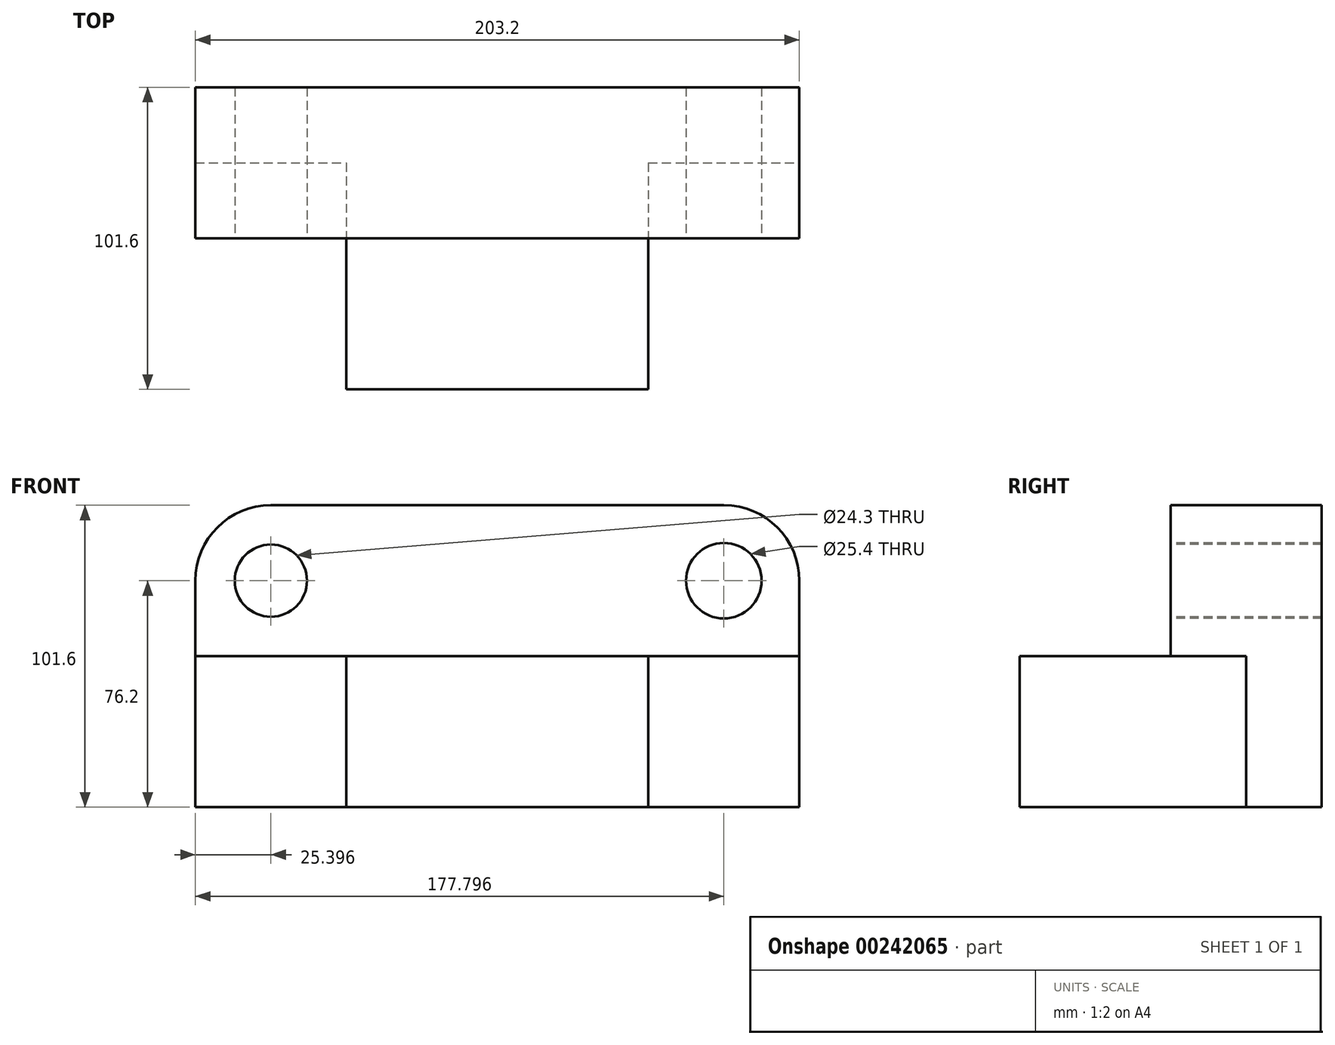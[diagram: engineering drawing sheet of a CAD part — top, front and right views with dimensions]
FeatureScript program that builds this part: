
annotation { "Feature Type Name" : "Feature", "Feature Type Description" : "" }
export const myFeature = defineFeature(function(context is Context, id is Id, definition is map)
    precondition{}
    {
        {
            var Q0;
            Q0=qCreatedBy(makeId("Top.planeOp"),FACE);
            var sketch = newSketch(context, id + "F0", { "sketchPlane" : qUnion([Q0])});
            skLineSegment(sketch, "E0.bottom", {"start": v(-154.2, -86.22) * mm, "end": v(49, -86.22) * mm});
            skLineSegment(sketch, "E0.top", {"start": v(-154.2, 15.38) * mm, "end": v(49, 15.38) * mm});
            skLineSegment(sketch, "E0.left", {"start": v(-154.2, -86.22) * mm, "end": v(-154.2, 15.38) * mm});
            skLineSegment(sketch, "E0.right", {"start": v(49, -86.22) * mm, "end": v(49, 15.38) * mm});
            skSolve(sketch);
        }
        {
            var Q0;
            Q0 = qSketchRegion(id + "F0", true);
            extrude(context, id + "F1", {"entities" : qUnion([Q0]), "depth" : 76.2 * mm});
        }
        {
            var Q0;
            Q0=makeQuery(id+"F1.opExtrude","SWEPT_FACE",FACE,{"disambiguationData":[OSD([sQuery(id+"F0.wireOp",EDGE,"E0.bottom")])]});
            var sketch = newSketch(context, id + "F2", { "sketchPlane" : qUnion([Q0])});
            skLineSegment(sketch, "E1", {"start": v(49, 0) * mm, "end": v(-1.8, 0) * mm});
            skLineSegment(sketch, "E2", {"start": v(-1.8, 0) * mm, "end": v(-1.8, 50.8) * mm});
            skLineSegment(sketch, "E3", {"start": v(-1.8, 50.8) * mm, "end": v(49, 50.8) * mm});
            skLineSegment(sketch, "E4", {"start": v(49, 50.8) * mm, "end": v(49, 0) * mm});
            skSolve(sketch);
        }
        {
            var Q0;
            Q0 = qSketchRegion(id + "F2", true);
            extrude(context, id + "F3", {"entities" : qUnion([Q0]), "operationType" : NewBodyOperationType.REMOVE, "oppositeDirection" : true, "depth" : 76.2 * mm});
        }
        {
            var Q0;
            Q0=makeQuery(id+"F1.opExtrude","SWEPT_FACE",FACE,{"disambiguationData":[OSD([sQuery(id+"F0.wireOp",EDGE,"E0.bottom")])]});
            var sketch = newSketch(context, id + "F4", { "sketchPlane" : qUnion([Q0])});
            skLineSegment(sketch, "E5", {"start": v(-1.8, 50.8) * mm, "end": v(-1.8, 76.2) * mm});
            skLineSegment(sketch, "E6", {"start": v(-1.8, 76.2) * mm, "end": v(49, 76.2) * mm});
            skLineSegment(sketch, "E7", {"start": v(-1.8, 50.8) * mm, "end": v(49, 50.8) * mm});
            skLineSegment(sketch, "E8", {"start": v(49, 76.2) * mm, "end": v(49, 50.8) * mm});
            skSolve(sketch);
        }
        {
            var Q0;
            Q0 = qSketchRegion(id + "F4", true);
            extrude(context, id + "F5", {"entities" : qUnion([Q0]), "operationType" : NewBodyOperationType.REMOVE, "oppositeDirection" : true, "depth" : 50.8 * mm});
        }
        {
            var Q0;
            Q0=makeQuery(id+"F1.opExtrude","SWEPT_FACE",FACE,{"disambiguationData":[OSD([sQuery(id+"F0.wireOp",EDGE,"E0.bottom")])]});
            var sketch = newSketch(context, id + "F6", { "sketchPlane" : qUnion([Q0])});
            skLineSegment(sketch, "E9", {"start": v(-154.2, 76.2) * mm, "end": v(-154.2, 50.8) * mm});
            skLineSegment(sketch, "E10", {"start": v(-154.2, 50.8) * mm, "end": v(-1.8, 50.8) * mm});
            skLineSegment(sketch, "E11", {"start": v(-1.8, 76.2) * mm, "end": v(-1.8, 50.8) * mm});
            skLineSegment(sketch, "E12", {"start": v(-154.2, 76.2) * mm, "end": v(-1.8, 76.2) * mm});
            skSolve(sketch);
        }
        {
            var Q0;
            Q0 = qSketchRegion(id + "F6", true);
            extrude(context, id + "F7", {"entities" : qUnion([Q0]), "operationType" : NewBodyOperationType.REMOVE, "oppositeDirection" : true, "depth" : 50.8 * mm});
        }
        {
            var Q0;
            Q0=makeQuery(id+"F1.opExtrude","SWEPT_FACE",FACE,{"disambiguationData":[OSD([sQuery(id+"F0.wireOp",EDGE,"E0.bottom")])]});
            var sketch = newSketch(context, id + "F8", { "sketchPlane" : qUnion([Q0])});
            skLineSegment(sketch, "E13", {"start": v(-154.2, 50.8) * mm, "end": v(-154.2, 0) * mm});
            skLineSegment(sketch, "E14", {"start": v(-154.2, 50.8) * mm, "end": v(-103.4, 50.8) * mm});
            skLineSegment(sketch, "E15", {"start": v(-103.4, 50.8) * mm, "end": v(-103.4, 0) * mm});
            skLineSegment(sketch, "E16", {"start": v(-154.2, 0) * mm, "end": v(-103.4, 0) * mm});
            skSolve(sketch);
        }
        {
            var Q0;
            Q0 = qSketchRegion(id + "F8", true);
            extrude(context, id + "F9", {"entities" : qUnion([Q0]), "operationType" : NewBodyOperationType.REMOVE, "oppositeDirection" : true, "depth" : 76.2 * mm});
        }
        {
            var Q0;
            Q0=makeQuery(id+"F1.opExtrude","CAP_FACE",FACE,{"disambiguationData":[OSD([sQuery(id+"F0.wireOp",EDGE,"E0.bottom"),sQuery(id+"F0.wireOp",EDGE,"E0.top"),sQuery(id+"F0.wireOp",EDGE,"E0.left"),sQuery(id+"F0.wireOp",EDGE,"E0.right")])],"isStart":false});
            var sketch = newSketch(context, id + "F10", { "sketchPlane" : qUnion([Q0])});
            skLineSegment(sketch, "E17.bottom", {"start": v(-154.2, -35.42) * mm, "end": v(49, -35.42) * mm});
            skLineSegment(sketch, "E17.top", {"start": v(-154.2, 15.38) * mm, "end": v(49, 15.38) * mm});
            skLineSegment(sketch, "E17.left", {"start": v(-154.2, -35.42) * mm, "end": v(-154.2, 15.38) * mm});
            skLineSegment(sketch, "E17.right", {"start": v(49, -35.42) * mm, "end": v(49, 15.38) * mm});
            skSolve(sketch);
        }
        {
            var Q0;
            Q0 = qSketchRegion(id + "F10", true);
            extrude(context, id + "F11", {"entities" : qUnion([Q0]), "operationType" : NewBodyOperationType.ADD, "depth" : 25.4 * mm});
        }
        {
            var Q0;
            Q0=makeQuery(id+"F11.opExtrude","CAP_EDGE",EDGE,{"disambiguationData":[OSD([sQuery(id+"F10.wireOp",EDGE,"E17.left")])],"isStart":false});
            fillet(context, id + "F12", {"entities" : qUnion([Q0]), "radius" : 25.4 * mm, "tangentPropagation" : true, "allowEdgeOverflow" : false});
        }
        {
            var Q0;
            Q0=makeQuery(id+"F11.opExtrude","CAP_EDGE",EDGE,{"disambiguationData":[OSD([sQuery(id+"F10.wireOp",EDGE,"E17.right")])],"isStart":false});
            fillet(context, id + "F13", {"entities" : qUnion([Q0]), "radius" : 25.4 * mm, "tangentPropagation" : true, "allowEdgeOverflow" : false});
        }
        {
            var Q0;
            Q0=makeQuery(id+"F11.boolean.opBoolean","MERGE",FACE,{"derivedFrom":[makeQuery(id+"F7.boolean.opBoolean","MERGE",FACE,{"derivedFrom":[makeQuery(id+"F5.boolean.opBoolean","COPY",FACE,{"derivedFrom":makeQuery(id+"F5.opExtrude","CAP_FACE",FACE,{"disambiguationData":[OSD([sQuery(id+"F4.wireOp",EDGE,"E5"),sQuery(id+"F4.wireOp",EDGE,"E6"),sQuery(id+"F4.wireOp",EDGE,"E7"),sQuery(id+"F4.wireOp",EDGE,"E8")])],"isStart":false})}),makeQuery(id+"F7.opExtrude","CAP_FACE",FACE,{"disambiguationData":[OSD([sQuery(id+"F6.wireOp",EDGE,"E9"),sQuery(id+"F6.wireOp",EDGE,"E10"),sQuery(id+"F6.wireOp",EDGE,"E11"),sQuery(id+"F6.wireOp",EDGE,"E12")])],"isStart":false})]}),makeQuery(id+"F11.opExtrude","SWEPT_FACE",FACE,{"disambiguationData":[OSD([sQuery(id+"F10.wireOp",EDGE,"E17.bottom")])]})]});
            var sketch = newSketch(context, id + "F14", { "sketchPlane" : qUnion([Q0])});
            skCircle(sketch, "E18", {"center": v(-128.8, 76.2) * mm, "radius": 12.15 * mm});
            skSolve(sketch);
        }
        {
            var Q0;
            Q0 = qSketchRegion(id + "F14", true);
            extrude(context, id + "F15", {"entities" : qUnion([Q0]), "operationType" : NewBodyOperationType.REMOVE, "oppositeDirection" : true, "depth" : 76.2 * mm});
        }
        {
            var Q0;
            Q0=makeQuery(id+"F11.boolean.opBoolean","MERGE",FACE,{"derivedFrom":[makeQuery(id+"F7.boolean.opBoolean","MERGE",FACE,{"derivedFrom":[makeQuery(id+"F5.boolean.opBoolean","COPY",FACE,{"derivedFrom":makeQuery(id+"F5.opExtrude","CAP_FACE",FACE,{"disambiguationData":[OSD([sQuery(id+"F4.wireOp",EDGE,"E5"),sQuery(id+"F4.wireOp",EDGE,"E6"),sQuery(id+"F4.wireOp",EDGE,"E7"),sQuery(id+"F4.wireOp",EDGE,"E8")])],"isStart":false})}),makeQuery(id+"F7.opExtrude","CAP_FACE",FACE,{"disambiguationData":[OSD([sQuery(id+"F6.wireOp",EDGE,"E9"),sQuery(id+"F6.wireOp",EDGE,"E10"),sQuery(id+"F6.wireOp",EDGE,"E11"),sQuery(id+"F6.wireOp",EDGE,"E12")])],"isStart":false})]}),makeQuery(id+"F11.opExtrude","SWEPT_FACE",FACE,{"disambiguationData":[OSD([sQuery(id+"F10.wireOp",EDGE,"E17.bottom")])]})]});
            var sketch = newSketch(context, id + "F16", { "sketchPlane" : qUnion([Q0])});
            skCircle(sketch, "E19", {"center": v(23.6, 76.2) * mm, "radius": 12.7 * mm});
            skSolve(sketch);
        }
        {
            var Q0;
            Q0 = qSketchRegion(id + "F16", true);
            extrude(context, id + "F17", {"entities" : qUnion([Q0]), "operationType" : NewBodyOperationType.REMOVE, "endBound" : BoundingType.THROUGH_ALL, "oppositeDirection" : true, "depth" : 50.8 * mm});
        }
    });
